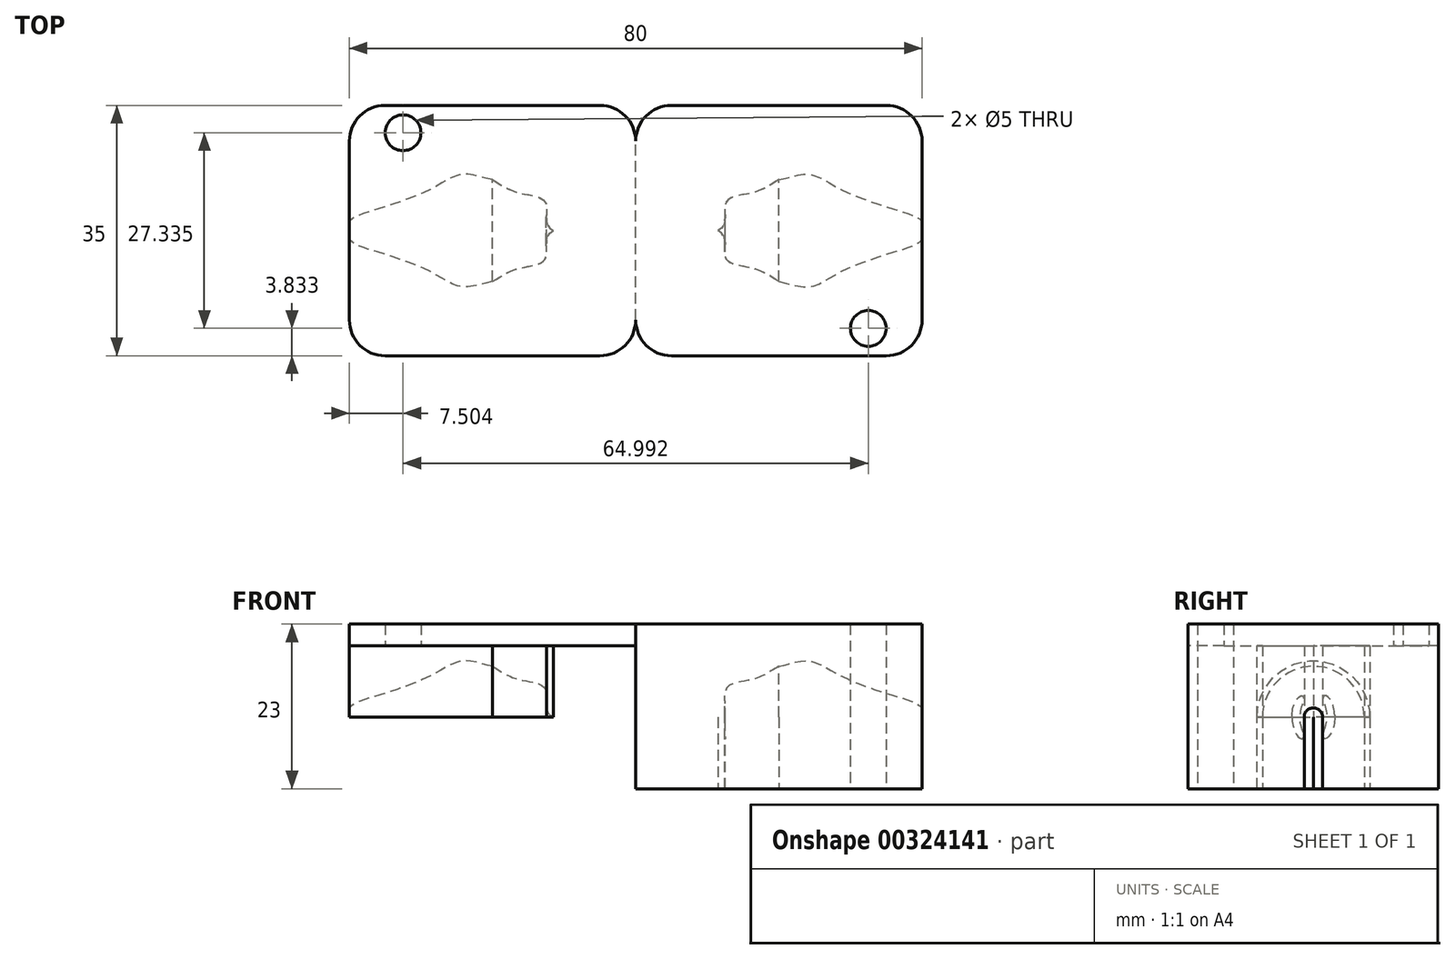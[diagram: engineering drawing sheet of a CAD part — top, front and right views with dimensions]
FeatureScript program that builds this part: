
annotation { "Feature Type Name" : "Feature", "Feature Type Description" : "" }
export const myFeature = defineFeature(function(context is Context, id is Id, definition is map)
    precondition{}
    {
        {
            var Q0;
            Q0=qCreatedBy(makeId("Top.planeOp"),FACE);
            var sketch = newSketch(context, id + "F0", { "sketchPlane" : qUnion([Q0])});
            skLineSegment(sketch, "E0.bottom", {"start": v(15, -17.5) * mm, "end": v(-15, -17.5) * mm});
            skLineSegment(sketch, "E0.top", {"start": v(15, 17.5) * mm, "end": v(-15, 17.5) * mm});
            skLineSegment(sketch, "E0.left", {"start": v(20, -12.5) * mm, "end": v(20, 12.5) * mm});
            skLineSegment(sketch, "E0.right", {"start": v(-20, -12.5) * mm, "end": v(-20, 12.5) * mm});
            skPoint(sketch, "E0.middle", {"position": v(0, 0) * mm});
            skCircle(sketch, "E1", {"center": v(12.5, 13.67) * mm, "radius": 2.5 * mm});
            skCircle(sketch, "E2.MirrorC", {"center": v(12.5, -13.67) * mm, "radius": 2.5 * mm});
            skFitSpline(sketch, "E3", {"points": [v(0, 7.1) * mm, v(4.36, 7.84) * mm, v(8.28, 5.96) * mm, v(15.52, 3.17) * mm, v(20, 1.29) * mm, v(20, 0) * mm], "startDerivative": vector(25.41, 5.65) * mm, "endDerivative": vector(-3.6, -12.86) * mm});
            skFitSpline(sketch, "E4.MirrorCS", {"points": [v(0, -7.1) * mm, v(4.36, -7.84) * mm, v(8.28, -5.96) * mm, v(15.52, -3.17) * mm, v(20, -1.29) * mm, v(20, 0) * mm], "startDerivative": vector(25.41, -5.65) * mm, "endDerivative": vector(-3.6, 12.86) * mm});
            skPoint(sketch, "E5.visualSharp", {"position": v(-20, 17.5) * mm});
            skArc(sketch, "E5.filletArc", {"start": v(-15, 17.5) * mm, "mid": v(-18.54, 16.04) * mm, "end": v(-20, 12.5) * mm});
            skPoint(sketch, "E6.visualSharp", {"position": v(20, 17.5) * mm});
            skArc(sketch, "E6.filletArc", {"start": v(20, 12.5) * mm, "mid": v(18.54, 16.04) * mm, "end": v(15, 17.5) * mm});
            skPoint(sketch, "E7.visualSharp", {"position": v(20, -17.5) * mm});
            skArc(sketch, "E7.filletArc", {"start": v(15, -17.5) * mm, "mid": v(18.54, -16.04) * mm, "end": v(20, -12.5) * mm});
            skPoint(sketch, "E8.visualSharp", {"position": v(-20, -17.5) * mm});
            skArc(sketch, "E8.filletArc", {"start": v(-20, -12.5) * mm, "mid": v(-18.54, -16.04) * mm, "end": v(-15, -17.5) * mm});
            skLineSegment(sketch, "E9.MirrorCS", {"start": v(-55, 17.5) * mm, "end": v(-25, 17.5) * mm});
            skLineSegment(sketch, "E10.MirrorCS", {"start": v(-60, -12.5) * mm, "end": v(-60, 12.5) * mm});
            skLineSegment(sketch, "E11.MirrorCS", {"start": v(-55, -17.5) * mm, "end": v(-25, -17.5) * mm});
            skArc(sketch, "E12.MirrorCS", {"start": v(-55, -17.5) * mm, "mid": v(-58.54, -16.04) * mm, "end": v(-60, -12.5) * mm});
            skArc(sketch, "E13.MirrorCS", {"start": v(-20, -12.5) * mm, "mid": v(-21.46, -16.04) * mm, "end": v(-25, -17.5) * mm});
            skArc(sketch, "E14.MirrorCS", {"start": v(-25, 17.5) * mm, "mid": v(-21.46, 16.04) * mm, "end": v(-20, 12.5) * mm});
            skFitSpline(sketch, "E15.MirrorCS", {"points": [v(-40, 7.1) * mm, v(-44.36, 7.84) * mm, v(-48.28, 5.96) * mm, v(-55.52, 3.17) * mm, v(-60, 1.29) * mm, v(-60, 0) * mm], "startDerivative": vector(-25.41, 5.65) * mm, "endDerivative": vector(3.6, -12.86) * mm});
            skFitSpline(sketch, "E16.MirrorCS", {"points": [v(-40, -7.1) * mm, v(-44.36, -7.84) * mm, v(-48.28, -5.96) * mm, v(-55.52, -3.17) * mm, v(-60, -1.29) * mm, v(-60, 0) * mm], "startDerivative": vector(-25.41, -5.65) * mm, "endDerivative": vector(3.6, 12.86) * mm});
            skCircle(sketch, "E17.MirrorC", {"center": v(-52.5, -13.67) * mm, "radius": 2.5 * mm});
            skCircle(sketch, "E18.MirrorC", {"center": v(-52.5, 13.67) * mm, "radius": 2.5 * mm});
            skArc(sketch, "E19.MirrorCS", {"start": v(-60, 12.5) * mm, "mid": v(-58.54, 16.04) * mm, "end": v(-55, 17.5) * mm});
            skLineSegment(sketch, "E20", {"start": v(20, 0) * mm, "end": v(-8.5, 0) * mm});
            skLineSegment(sketch, "E21.MirrorCS", {"start": v(-60, 0) * mm, "end": v(-31.5, 0) * mm});
            skFitSpline(sketch, "E22", {"points": [v(-40, -7.1) * mm, v(-36.1, -5.22) * mm, v(-32.58, -3.83) * mm, v(-31.5, 0) * mm], "startDerivative": vector(13.76, 8.45) * mm, "endDerivative": vector(14.66, 6.65) * mm});
            skFitSpline(sketch, "E23.MirrorCS", {"points": [v(-40, 7.1) * mm, v(-36.1, 5.22) * mm, v(-32.58, 3.83) * mm, v(-31.5, 0) * mm], "startDerivative": vector(13.76, -8.45) * mm, "endDerivative": vector(14.66, -6.65) * mm});
            skFitSpline(sketch, "E24.MirrorCS", {"points": [v(0, -7.1) * mm, v(-3.9, -5.22) * mm, v(-7.42, -3.83) * mm, v(-8.5, 0) * mm], "startDerivative": vector(-13.76, 8.45) * mm, "endDerivative": vector(-14.66, 6.65) * mm});
            skFitSpline(sketch, "E25.MirrorCS", {"points": [v(0, 7.1) * mm, v(-3.9, 5.22) * mm, v(-7.42, 3.83) * mm, v(-8.5, 0) * mm], "startDerivative": vector(-13.76, -8.45) * mm, "endDerivative": vector(-14.66, -6.65) * mm});
            skLineSegment(sketch, "E26", {"start": v(-20, 12.5) * mm, "end": v(-20, -12.5) * mm});
            skSolve(sketch);
        }
        {
            var Q0;
            {var subQ1=sQuery(id+"F0.wireOp",EDGE,"s9bVcs6r-2fpT-YKaw-YGMu-SIAytN7dKQFH");Q0=makeQuery(id+"F0.imprint","IMPRINT",FACE,{"disambiguationData":[TD([[makeQuery(id+"F0.imprint","IMPRINT",EDGE,{"derivedFrom":subQ1}),1.0]])]});}
            var Q1;
            Q1=makeQuery(id+"F0.imprint","IMPRINT",FACE,{"disambiguationData":[TD([[makeQuery(id+"F0.imprint","IMPRINT",EDGE,{"derivedFrom":sQuery(id+"F0.wireOp",EDGE,"E0.bottom")}),-1.0]])]});
            var Q2;
            {var subQ0=sQuery(id+"F0.wireOp",EDGE,"E20");Q2=makeQuery(id+"F0.imprint","IMPRINT",FACE,{"disambiguationData":[TD([[makeQuery(id+"F0.imprint","IMPRINT",EDGE,{"derivedFrom":subQ0}),-1.0]])]});}
            var Q3;
            {var subQ0=sQuery(id+"F0.wireOp",EDGE,"E20");Q3=makeQuery(id+"F0.imprint","IMPRINT",FACE,{"disambiguationData":[TD([[makeQuery(id+"F0.imprint","IMPRINT",EDGE,{"derivedFrom":subQ0}),1.0]])]});}
            extrude(context, id + "F1", {"entities" : qUnion([Q0, Q1, Q2, Q3]), "depth" : 13 * mm});
        }
        {
            var Q0;
            Q0=makeQuery(id+"F0.imprint","IMPRINT",FACE,{"disambiguationData":[TD([[makeQuery(id+"F0.imprint","IMPRINT",EDGE,{"derivedFrom":sQuery(id+"F0.wireOp",EDGE,"E9.MirrorCS")}),-1.0]])]});
            var Q1;
            {var subQ0=sQuery(id+"F0.wireOp",EDGE,"E21.MirrorCS");Q1=makeQuery(id+"F0.imprint","IMPRINT",FACE,{"disambiguationData":[TD([[makeQuery(id+"F0.imprint","IMPRINT",EDGE,{"derivedFrom":subQ0}),-1.0]])]});}
            var Q2;
            {var subQ0=sQuery(id+"F0.wireOp",EDGE,"E21.MirrorCS");Q2=makeQuery(id+"F0.imprint","IMPRINT",FACE,{"disambiguationData":[TD([[makeQuery(id+"F0.imprint","IMPRINT",EDGE,{"derivedFrom":subQ0}),1.0]])]});}
            extrude(context, id + "F2", {"entities" : qUnion([Q0, Q1, Q2]), "operationType" : NewBodyOperationType.ADD, "depth" : 13 * mm});
        }
        {
            var Q0;
            Q0=makeQuery(id+"F0.imprint","IMPRINT",FACE,{"disambiguationData":[TD([[makeQuery(id+"F0.imprint","IMPRINT",EDGE,{"derivedFrom":sQuery(id+"F0.wireOp",EDGE,"E1")}),1.0]])]});
            var Q1;
            Q1=makeQuery(id+"F0.imprint","IMPRINT",FACE,{"disambiguationData":[TD([[makeQuery(id+"F0.imprint","IMPRINT",EDGE,{"derivedFrom":sQuery(id+"F0.wireOp",EDGE,"E2.MirrorC")}),-1.0]])]});
            extrude(context, id + "F3", {"entities" : qUnion([Q0, Q1]), "operationType" : NewBodyOperationType.ADD, "endBound" : BoundingType.SYMMETRIC, "depth" : 26 * mm});
        }
        {
            var Q0;
            {var subQ0=sQuery(id+"F0.wireOp",EDGE,"E21.MirrorCS");Q0=makeQuery(id+"F0.imprint","IMPRINT",FACE,{"disambiguationData":[TD([[makeQuery(id+"F0.imprint","IMPRINT",EDGE,{"derivedFrom":subQ0}),-1.0]])]});}
            var Q1;
            {var subQ0=sQuery(id+"F0.wireOp",EDGE,"E20");Q1=makeQuery(id+"F0.imprint","IMPRINT",FACE,{"disambiguationData":[TD([[makeQuery(id+"F0.imprint","IMPRINT",EDGE,{"derivedFrom":subQ0}),1.0]])]});}
            var Q2;
            Q2=sQuery(id+"F0.wireOp",EDGE,"E21.MirrorCS");
            revolve(context, id + "F4", {"operationType" : NewBodyOperationType.REMOVE, "entities" : qUnion([Q0, Q1]), "axis" : qUnion([Q2]), "revolveType" : RevolveType.FULL});
        }
        {
            var Q0;
            Q0=makeQuery(id+"F0.imprint","IMPRINT",FACE,{"disambiguationData":[TD([[makeQuery(id+"F0.imprint","IMPRINT",EDGE,{"derivedFrom":sQuery(id+"F0.wireOp",EDGE,"E18.MirrorC")}),-1.0]])]});
            var Q1;
            Q1=makeQuery(id+"F0.imprint","IMPRINT",FACE,{"disambiguationData":[TD([[makeQuery(id+"F0.imprint","IMPRINT",EDGE,{"derivedFrom":sQuery(id+"F0.wireOp",EDGE,"E17.MirrorC")}),1.0]])]});
            extrude(context, id + "F5", {"entities" : qUnion([Q0, Q1]), "operationType" : NewBodyOperationType.ADD, "depth" : 13 * mm});
        }
        {
            var Q0;
            Q0=makeQuery(id+"F0.imprint","IMPRINT",FACE,{"disambiguationData":[TD([[makeQuery(id+"F0.imprint","IMPRINT",EDGE,{"derivedFrom":sQuery(id+"F0.wireOp",EDGE,"E18.MirrorC")}),-1.0]])]});
            var Q1;
            Q1=makeQuery(id+"F0.imprint","IMPRINT",FACE,{"disambiguationData":[TD([[makeQuery(id+"F0.imprint","IMPRINT",EDGE,{"derivedFrom":sQuery(id+"F0.wireOp",EDGE,"E17.MirrorC")}),1.0]])]});
            extrude(context, id + "F6", {"entities" : qUnion([Q0, Q1]), "operationType" : NewBodyOperationType.REMOVE, "depth" : 10 * mm});
        }
        {
            var Q0;
            Q0=makeQuery(id+"F3.opExtrude","CAP_FACE",FACE,{"disambiguationData":[OSD([sQuery(id+"F0.wireOp",EDGE,"E2.MirrorC")])],"isStart":true});
            var Q1;
            Q1=makeQuery(id+"F3.opExtrude","CAP_FACE",FACE,{"disambiguationData":[OSD([sQuery(id+"F0.wireOp",EDGE,"E1")])],"isStart":true});
            extrude(context, id + "F7", {"entities" : qUnion([Q0, Q1]), "operationType" : NewBodyOperationType.REMOVE, "oppositeDirection" : true, "depth" : 3 * mm});
        }
    });
